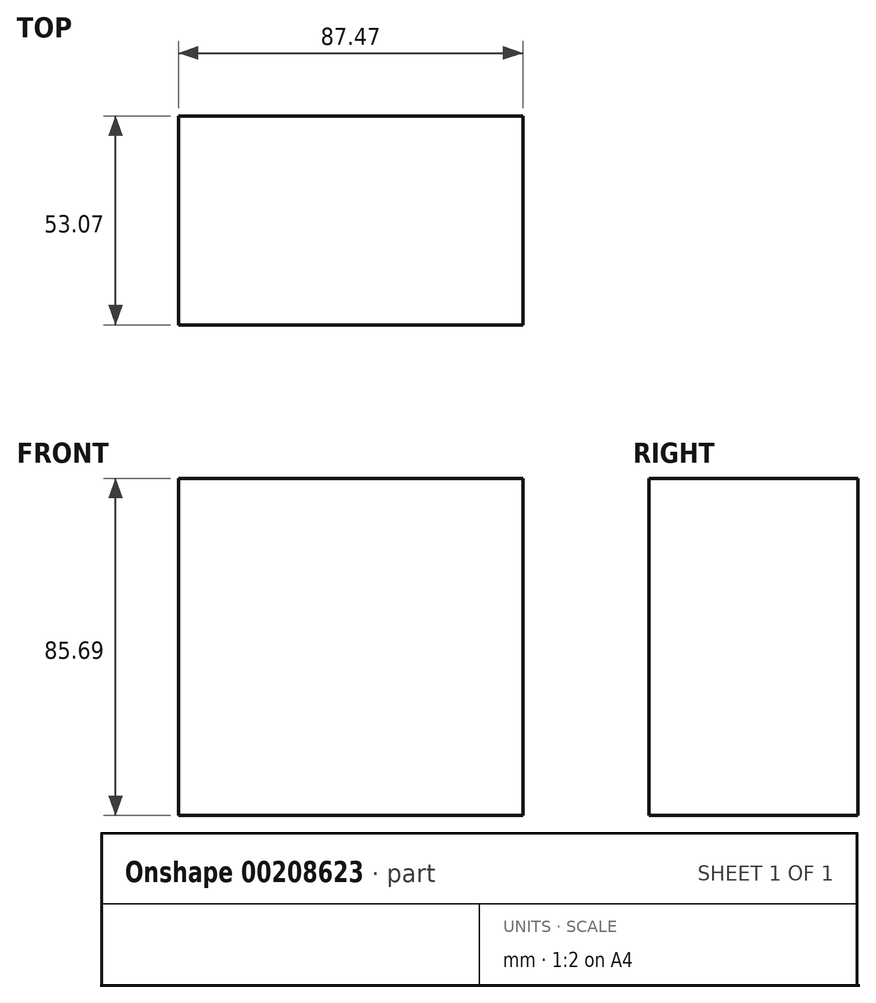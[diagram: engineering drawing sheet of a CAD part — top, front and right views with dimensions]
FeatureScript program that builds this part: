
annotation { "Feature Type Name" : "Feature", "Feature Type Description" : "" }
export const myFeature = defineFeature(function(context is Context, id is Id, definition is map)
    precondition{}
    {
        {
            var Q0;
            Q0=qCreatedBy(makeId("Front.planeOp"),FACE);
            var sketch = newSketch(context, id + "F0", { "sketchPlane" : qUnion([Q0])});
            skLineSegment(sketch, "E0.bottom", {"start": v(-35.84, 27.63) * mm, "end": v(51.63, 27.63) * mm});
            skLineSegment(sketch, "E0.top", {"start": v(-35.84, -58.06) * mm, "end": v(51.63, -58.06) * mm});
            skLineSegment(sketch, "E0.left", {"start": v(-35.84, 27.63) * mm, "end": v(-35.84, -58.06) * mm});
            skLineSegment(sketch, "E0.right", {"start": v(51.63, 27.63) * mm, "end": v(51.63, -58.06) * mm});
            skSolve(sketch);
        }
        {
            var Q0;
            Q0 = qSketchRegion(id + "F0", true);
            var Q1;
            Q1=makeQuery(id+"F0.imprint","IMPRINT",FACE,{"disambiguationData":[TD([[makeQuery(id+"F0.imprint","IMPRINT",EDGE,{"derivedFrom":sQuery(id+"F0.wireOp",EDGE,"E0.bottom")}),-1.0]])]});
            extrude(context, id + "F1", {"entities" : qUnion([Q0, Q1]), "depth" : 53.07 * mm});
        }
    });
